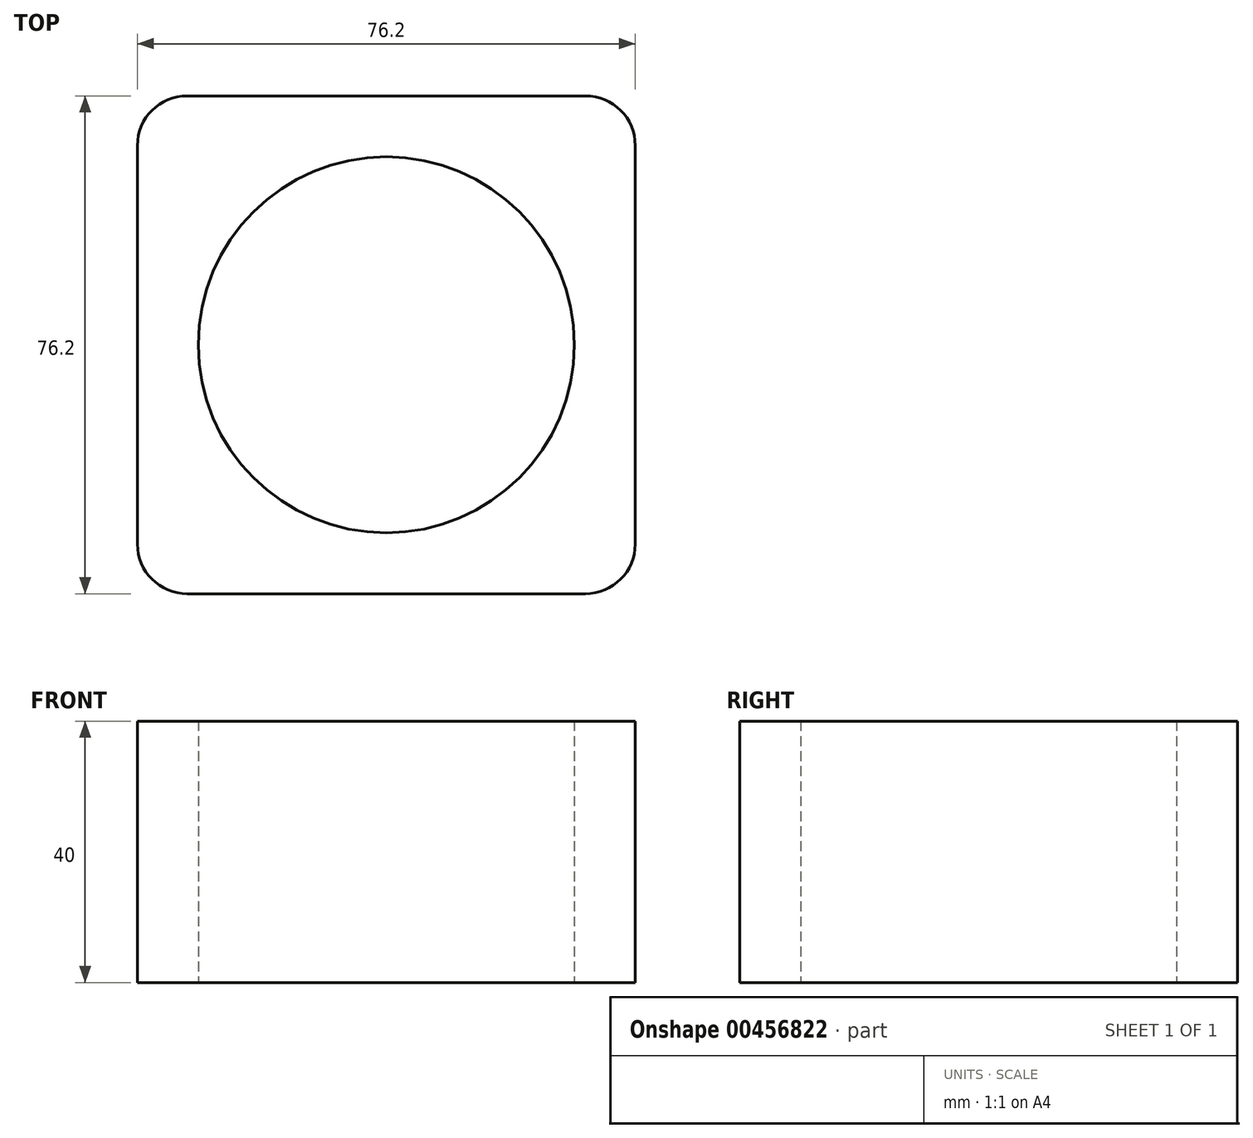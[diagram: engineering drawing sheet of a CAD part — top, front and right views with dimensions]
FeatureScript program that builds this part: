
annotation { "Feature Type Name" : "Feature", "Feature Type Description" : "" }
export const myFeature = defineFeature(function(context is Context, id is Id, definition is map)
    precondition{}
    {
        {
            var Q0;
            Q0=qCreatedBy(makeId("Top.planeOp"),FACE);
            var sketch = newSketch(context, id + "F0", { "sketchPlane" : qUnion([Q0])});
            skLineSegment(sketch, "E0.bottom", {"start": v(-30.48, 38.1) * mm, "end": v(30.48, 38.1) * mm});
            skLineSegment(sketch, "E0.top", {"start": v(-30.48, -38.1) * mm, "end": v(30.48, -38.1) * mm});
            skLineSegment(sketch, "E0.left", {"start": v(-38.1, 30.48) * mm, "end": v(-38.1, -30.48) * mm});
            skLineSegment(sketch, "E0.right", {"start": v(38.1, 30.48) * mm, "end": v(38.1, -30.48) * mm});
            skPoint(sketch, "E0.middle", {"position": v(0, 0) * mm});
            skPoint(sketch, "E1.visualSharp", {"position": v(-38.1, 38.1) * mm});
            skArc(sketch, "E1.filletArc", {"start": v(-30.48, 38.1) * mm, "mid": v(-35.87, 35.87) * mm, "end": v(-38.1, 30.48) * mm});
            skPoint(sketch, "E2.visualSharp", {"position": v(38.1, 38.1) * mm});
            skArc(sketch, "E2.filletArc", {"start": v(38.1, 30.48) * mm, "mid": v(35.87, 35.87) * mm, "end": v(30.48, 38.1) * mm});
            skPoint(sketch, "E3.visualSharp", {"position": v(-38.1, -38.1) * mm});
            skArc(sketch, "E3.filletArc", {"start": v(-38.1, -30.48) * mm, "mid": v(-35.87, -35.87) * mm, "end": v(-30.48, -38.1) * mm});
            skPoint(sketch, "E4.visualSharp", {"position": v(38.1, -38.1) * mm});
            skArc(sketch, "E4.filletArc", {"start": v(30.48, -38.1) * mm, "mid": v(35.87, -35.87) * mm, "end": v(38.1, -30.48) * mm});
            skCircle(sketch, "E5", {"center": v(0, 0) * mm, "radius": 28.78 * mm});
            skPoint(sketch, "E6", {"position": v(26.14, -24.54) * mm});
            skPoint(sketch, "E7", {"position": v(30.48, 27.73) * mm});
            skSolve(sketch);
        }
        {
            var Q0;
            Q0 = qSketchRegion(id + "F0", true);
            var Q1;
            Q1=makeQuery(id+"F0.imprint","IMPRINT",FACE,{"disambiguationData":[TD([[makeQuery(id+"F0.imprint","IMPRINT",EDGE,{"derivedFrom":sQuery(id+"F0.wireOp",EDGE,"E0.bottom")}),-1.0]])]});
            extrude(context, id + "F1", {"entities" : qUnion([Q0, Q1]), "depth" : 40 * mm});
        }
        {
            var Q0;
            Q0=makeQuery(id+"F1.opExtrude","CAP_FACE",FACE,{"disambiguationData":[OSD([sQuery(id+"F0.wireOp",EDGE,"E0.bottom"),sQuery(id+"F0.wireOp",EDGE,"E0.top"),sQuery(id+"F0.wireOp",EDGE,"E0.left"),sQuery(id+"F0.wireOp",EDGE,"E0.right"),sQuery(id+"F0.wireOp",EDGE,"E1.filletArc"),sQuery(id+"F0.wireOp",EDGE,"E2.filletArc"),sQuery(id+"F0.wireOp",EDGE,"E3.filletArc"),sQuery(id+"F0.wireOp",EDGE,"E4.filletArc"),sQuery(id+"F0.wireOp",EDGE,"E5")])],"isStart":true});
            extrude(context, id + "F2", {"entities" : qUnion([Q0]), "operationType" : NewBodyOperationType.ADD, "oppositeDirection" : true, "depth" : 10 * mm});
        }
        {
            var Q0;
            Q0 = qSketchRegion(id + "F0", true);
            extrude(context, id + "F3", {"entities" : qUnion([Q0]), "operationType" : NewBodyOperationType.ADD, "depth" : 20 * mm});
        }
    });
